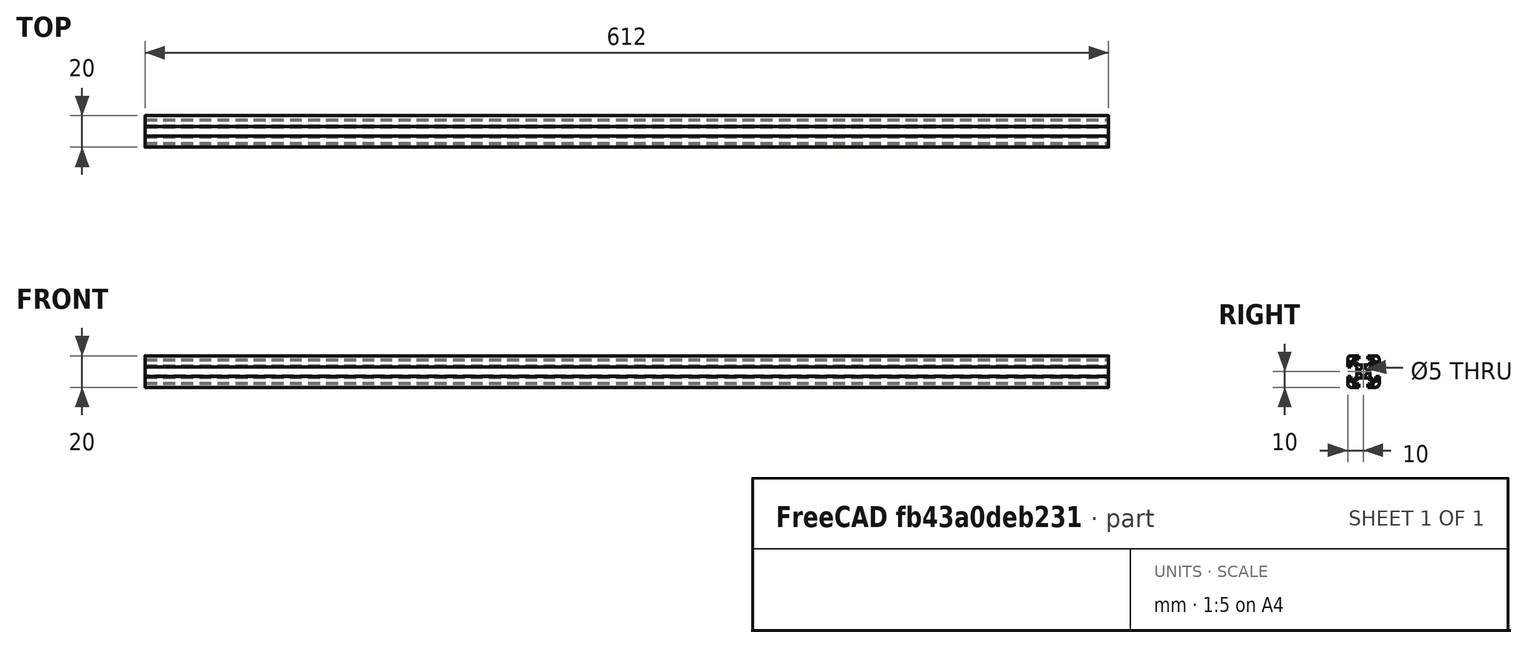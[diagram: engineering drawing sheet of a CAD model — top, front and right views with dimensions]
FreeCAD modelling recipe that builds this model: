
FCSTD DOCUMENT  (FreeCAD 0.19R24267 +99 (Git))
Label: 2020 Rail strut camera support 612mm
License: All rights reserved
LicenseURL: http://en.wikipedia.org/wiki/All_rights_reserved
objects: Sketcher::SketchObject×1, PartDesign::Pad×1, PartDesign::Body×1
note: 4 computed .brp shape members not serialized (recipe doc carries the construction recipe); baked Part::Feature solids carry a one-line shape summary decoded from their .brp

FEATURE [Sketcher::SketchObject] Sketch  label="Rail cross section"
  FullyConstrained = true
  MapMode = 5
  Placement = pos=(0,0,0) rot=(0.57735,0.57735,0.57735;2.0944rad)
  Support = -> [YZ_Plane]
  sketch-geometry (47):
    g0: ArcOfCircle CenterX=-8 CenterY=8 CenterZ=0 NormalX=0 NormalY=0 NormalZ=1 AngleXU=0 Radius=2 StartAngle=1.5708 EndAngle=3.14159
    g1: ArcOfCircle CenterX=-8 CenterY=-8 CenterZ=0 NormalX=0 NormalY=0 NormalZ=1 AngleXU=0 Radius=2 StartAngle=3.14159 EndAngle=4.71239
    g2: ArcOfCircle CenterX=8 CenterY=-8 CenterZ=0 NormalX=0 NormalY=0 NormalZ=1 AngleXU=0 Radius=2 StartAngle=4.71239 EndAngle=6.28319
    g3: ArcOfCircle CenterX=8 CenterY=8 CenterZ=0 NormalX=0 NormalY=0 NormalZ=1 AngleXU=0 Radius=2 StartAngle=2e-16 EndAngle=1.5708
    g4: Circle CenterX=0 CenterY=0 CenterZ=0 NormalX=0 NormalY=0 NormalZ=1 AngleXU=0 Radius=2.5
    g5: LineSegment StartX=-10 StartY=8 StartZ=0 EndX=-10 EndY=3 EndZ=0
    g6: LineSegment StartX=-10 StartY=-3 StartZ=0 EndX=-10 EndY=-8 EndZ=0
    g7: LineSegment StartX=-8 StartY=-10 StartZ=0 EndX=-3 EndY=-10 EndZ=0
    g8: LineSegment StartX=3 StartY=-10 StartZ=0 EndX=8 EndY=-10 EndZ=0
    g9: LineSegment StartX=10 StartY=-8 StartZ=0 EndX=10 EndY=-3 EndZ=0
    g10: LineSegment StartX=10 StartY=3 StartZ=0 EndX=10 EndY=8 EndZ=0
    g11: LineSegment StartX=-8 StartY=10 StartZ=0 EndX=-3 EndY=10 EndZ=0
    g12: LineSegment StartX=3 StartY=10 StartZ=0 EndX=8 EndY=10 EndZ=0
    g13: LineSegment StartX=-3 StartY=4 StartZ=0 EndX=3 EndY=4 EndZ=0
    g14: LineSegment StartX=4 StartY=3 StartZ=0 EndX=4 EndY=-3 EndZ=0
    g15: LineSegment StartX=3 StartY=-4 StartZ=0 EndX=-3 EndY=-4 EndZ=0
    g16: LineSegment StartX=-4 StartY=-3 StartZ=0 EndX=-4 EndY=3 EndZ=0
    g17: LineSegment StartX=-3 StartY=-4 StartZ=0 EndX=-7 EndY=-8 EndZ=0
    g18: LineSegment StartX=-3 StartY=-10 StartZ=0 EndX=-3 EndY=-8 EndZ=0
    g19: LineSegment StartX=3 StartY=-4 StartZ=0 EndX=7 EndY=-8 EndZ=0
    g20: LineSegment StartX=4 StartY=-3 StartZ=0 EndX=8 EndY=-7 EndZ=0
    g21: LineSegment StartX=8 StartY=-7 StartZ=0 EndX=8 EndY=-3 EndZ=0
    g22: LineSegment StartX=10 StartY=-3 StartZ=0 EndX=8 EndY=-3 EndZ=0
    g23: LineSegment StartX=4 StartY=3 StartZ=0 EndX=8 EndY=7 EndZ=0
    g24: LineSegment StartX=8 StartY=7 StartZ=0 EndX=8 EndY=3 EndZ=0
    g25: LineSegment StartX=8 StartY=3 StartZ=0 EndX=10 EndY=3 EndZ=0
    g26: LineSegment StartX=3 StartY=10 StartZ=0 EndX=3 EndY=8 EndZ=0
    g27: LineSegment StartX=3 StartY=8 StartZ=0 EndX=7 EndY=8 EndZ=0
    g28: LineSegment StartX=7 StartY=8 StartZ=0 EndX=3 EndY=4 EndZ=0
    g29: LineSegment StartX=-3 StartY=4 StartZ=0 EndX=-7 EndY=8 EndZ=0
    g30: LineSegment StartX=-7 StartY=8 StartZ=0 EndX=-3 EndY=8 EndZ=0
    g31: LineSegment StartX=-3 StartY=8 StartZ=0 EndX=-3 EndY=10 EndZ=0
    g32: LineSegment StartX=-4 StartY=3 StartZ=0 EndX=-8 EndY=7 EndZ=0
    g33: LineSegment StartX=-8 StartY=3 StartZ=0 EndX=-10 EndY=3 EndZ=0
    g34: LineSegment StartX=-10 StartY=-3 StartZ=0 EndX=-8 EndY=-3 EndZ=0
    g35: LineSegment StartX=-8 StartY=-7 StartZ=0 EndX=-4 EndY=-3 EndZ=0
    g36: LineSegment StartX=3 StartY=-10 StartZ=0 EndX=3 EndY=-8 EndZ=0
    g37: LineSegment StartX=3 StartY=-8 StartZ=0 EndX=7 EndY=-8 EndZ=0
    g38: LineSegment StartX=-3 StartY=-8 StartZ=0 EndX=-7 EndY=-8 EndZ=0
    g39: LineSegment StartX=-8 StartY=-7 StartZ=0 EndX=-8 EndY=-3 EndZ=0
    g40: LineSegment StartX=-8 StartY=3 StartZ=0 EndX=-8 EndY=7 EndZ=0
    g41: LineSegment StartX=-3 StartY=10 StartZ=0 EndX=3 EndY=10 EndZ=0
    g42: LineSegment StartX=10 StartY=3 StartZ=0 EndX=10 EndY=-3 EndZ=0
    g43: LineSegment StartX=3 StartY=-10 StartZ=0 EndX=-3 EndY=-10 EndZ=0
    g44: LineSegment StartX=-10 StartY=-3 StartZ=0 EndX=-10 EndY=3 EndZ=0
    g45: LineSegment StartX=-4 StartY=-3 StartZ=0 EndX=-3 EndY=-4 EndZ=0
    g46: LineSegment StartX=-8 StartY=-7 StartZ=0 EndX=-7 EndY=-8 EndZ=0
  constraints (128):
    c: Radius(g0) = 2  'ASSUMED EDGE RADIUS'
    c: Equal(g1,g2)
    c: Coincident(g4,g-1)
    c: Radius(g4) = 2.5  'CENTER HOLE'
    c: Vertical(g6)
    c: Horizontal(g7)
    c: Horizontal(g8)
    c: Vertical(g9)
    c: Vertical(g10)
    c: Horizontal(g11)
    c: Horizontal(g12)
    c: DistanceX(g0,g3) = 20  'RAIL WIDTH'
    c: Vertical(g5)
    c: DistanceY(g2,g3) = 20  'RAIL HEIGHT'
    c: DistanceX(g7,g8) = 6  'SLOT WIDTH'
    c: Equal(g8,g7)
    c: Equal(g7,g6)
    c: Equal(g5,g11)
    c: Equal(g12,g10)
    c: Tangent(g12,g3) = 1.5708
    c: Tangent(g10,g3) = -1.5708
    c: Tangent(g11,g0) = 1.5708
    c: Tangent(g5,g0) = -1.5708
    c: Tangent(g6,g1) = -1.5708
    c: Tangent(g7,g1) = -1.5708
    c: Tangent(g8,g2) = -1.5708
    c: Tangent(g9,g2) = -1.5708
    c: Symmetric(g3,g2,g-1)
    c: Symmetric(g0,g3,g-2)
    c: Horizontal(g13)
    c: Vertical(g14)
    c: Vertical(g16)
    c: Horizontal(g15)
    c: Equal(g16,g15)
    c: Equal(g15,g14)
    c: Coincident(g17,g15)
    c: Coincident(g18,g7)
    c: Vertical(g18)
    c: Coincident(g19,g15)
    c: Coincident(g20,g14)
    c: Coincident(g21,g20)
    c: Vertical(g21)
    c: Coincident(g22,g9)
    c: Coincident(g22,g21)
    c: Coincident(g23,g14)
    c: Coincident(g24,g23)
    c: Vertical(g24)
    c: Coincident(g25,g24)
    c: Coincident(g25,g10)
    c: Coincident(g26,g12)
    c: Vertical(g26)
    c: Coincident(g27,g26)
    c: Horizontal(g27)
    c: Coincident(g28,g27)
    c: Coincident(g28,g13)
    c: Coincident(g29,g13)
    c: Coincident(g30,g29)
    c: Horizontal(g30)
    c: Coincident(g31,g30)
    c: Coincident(g31,g11)
    c: Coincident(g32,g16)
    c: Coincident(g33,g5)
    c: Horizontal(g33)
    c: Coincident(g34,g6)
    c: Horizontal(g34)
    c: Coincident(g35,g16)
    c: Coincident(g36,g8)
    c: Vertical(g36)
    c: Coincident(g37,g36)
    c: Coincident(g37,g19)
    c: Coincident(g38,g18)
    c: Coincident(g38,g17)
    c: Horizontal(g38)
    c: Coincident(g39,g35)
    c: Coincident(g39,g34)
    c: Vertical(g39)
    c: Coincident(g40,g33)
    c: Coincident(g40,g32)
    c: Vertical(g40)
    c: Horizontal(g37)
    c: Horizontal(g25)
    c: Horizontal(g22)
    c: Equal(g38,g37)
    c: Equal(g37,g21)
    c: Equal(g21,g24)
    c: Equal(g24,g27)
    c: Equal(g27,g30)
    c: Equal(g30,g40)
    c: Equal(g40,g39)
    c: Vertical(g31)
    c: Equal(g31,g26)
    c: Equal(g26,g25)
    c: Equal(g25,g22)
    c: Equal(g22,g36)
    c: Equal(g36,g18)
    c: Equal(g18,g34)
    c: Equal(g34,g33)
    c: Equal(g32,g29)
    c: Equal(g29,g28)
    c: Equal(g28,g23)
    c: Equal(g23,g20)
    c: Equal(g20,g19)
    c: Equal(g19,g17)
    c: Equal(g17,g35)
    c: Coincident(g41,g11)
    c: Coincident(g41,g12)
    c: Coincident(g42,g10)
    c: Coincident(g42,g9)
    c: Coincident(g43,g8)
    c: Coincident(g43,g7)
    c: Horizontal(g43)
    c: Coincident(g44,g6)
    c: Coincident(g44,g5)
    c: Vertical(g44)
    c: Horizontal(g41)
    c: DistanceY(g8,g15) = 6  'ASSUMED SLOT DEPTH'
    c: Equal(g43,g15)
    c: Equal(g16,g13)
    c: Equal(g44,g43)
    c: Equal(g43,g42)
    c: Equal(g42,g41)
    c: Vertical(g42)
    c: DistanceY(g36,g36) = 2  'ASSUMED WALL THICKNESS'
    c: Coincident(g45,g16)
    c: Coincident(g45,g15)
    c: Coincident(g46,g35)
    c: Coincident(g46,g17)
    c: Equal(g45,g46)
FEATURE [PartDesign::Pad] Pad  label="Length"
  Direction = (1,1,1)
  Length = 612
  Length2 = 100
  Placement = pos=(0,0,0) rot=(0.57735,0.57735,0.57735;2.0944rad)
  Profile = -> Sketch
  Type = 0
FEATURE [PartDesign::Body] Body
  Group = -> [Sketch,Pad]
  Origin = -> Origin
  Tip = -> Pad
